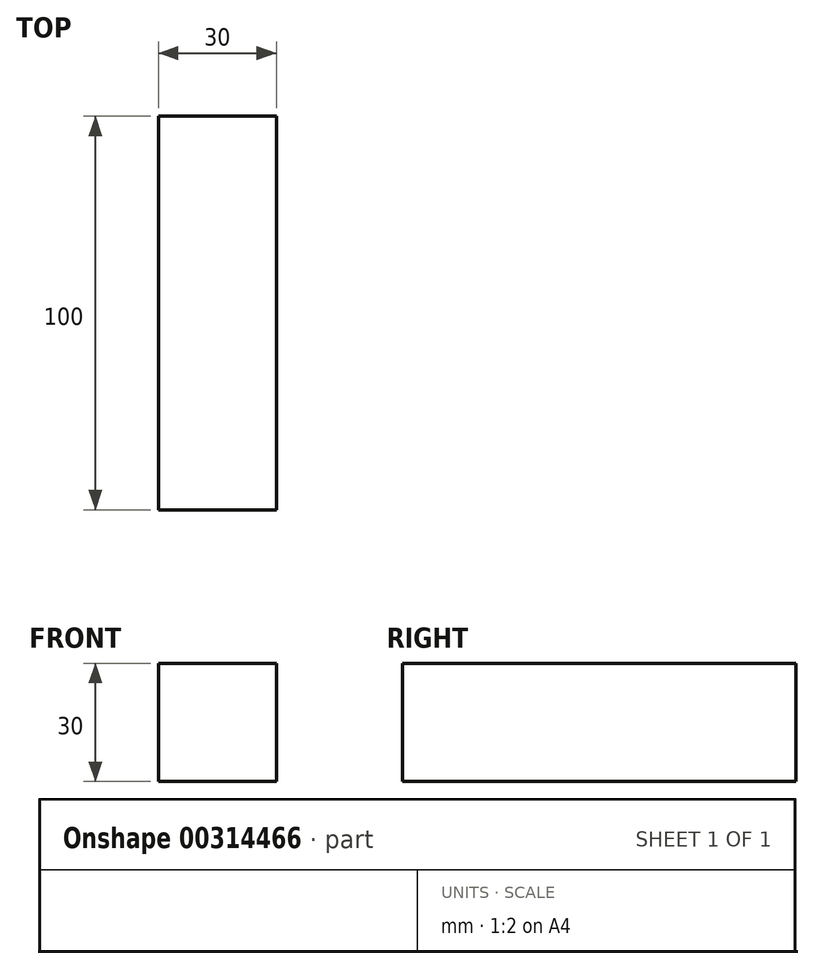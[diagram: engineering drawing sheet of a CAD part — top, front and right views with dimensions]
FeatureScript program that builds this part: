
annotation { "Feature Type Name" : "Feature", "Feature Type Description" : "" }
export const myFeature = defineFeature(function(context is Context, id is Id, definition is map)
    precondition{}
    {
        {
            var Q0;
            Q0=qCreatedBy(makeId("Top.planeOp"),FACE);
            var sketch = newSketch(context, id + "F0", { "sketchPlane" : qUnion([Q0])});
            skLineSegment(sketch, "E0.bottom", {"start": v(15, -50) * mm, "end": v(-15, -50) * mm});
            skLineSegment(sketch, "E0.top", {"start": v(15, 50) * mm, "end": v(-15, 50) * mm});
            skLineSegment(sketch, "E0.left", {"start": v(15, -50) * mm, "end": v(15, 50) * mm});
            skLineSegment(sketch, "E0.right", {"start": v(-15, -50) * mm, "end": v(-15, 50) * mm});
            skPoint(sketch, "E0.middle", {"position": v(0, 0) * mm});
            skSolve(sketch);
        }
        {
            var Q0;
            Q0 = qSketchRegion(id + "F0", true);
            extrude(context, id + "F1", {"entities" : qUnion([Q0]), "depth" : 30 * mm});
        }
    });
